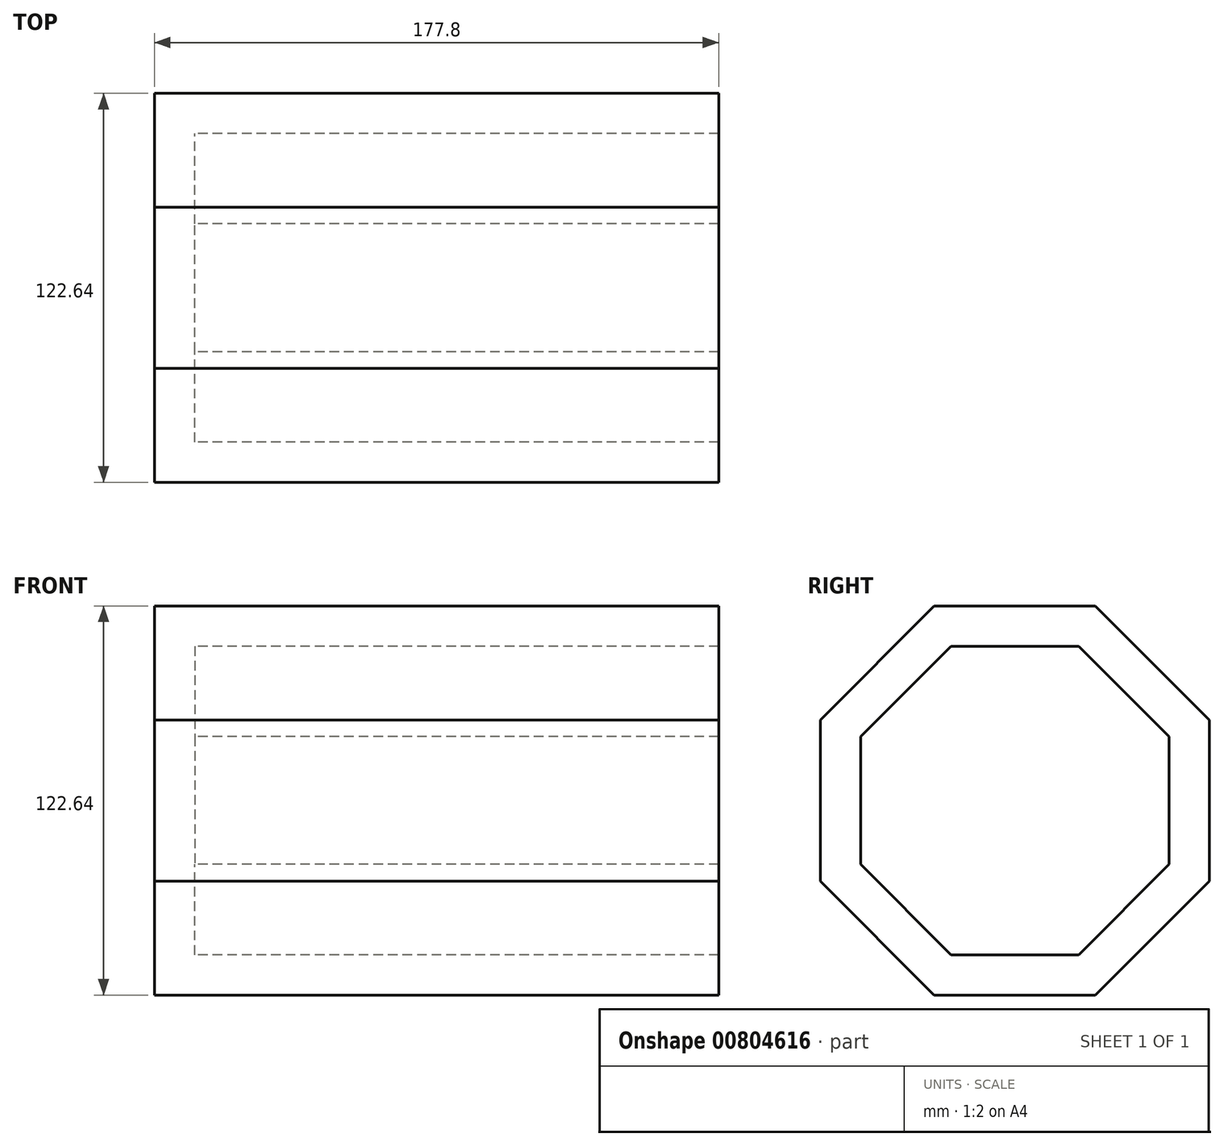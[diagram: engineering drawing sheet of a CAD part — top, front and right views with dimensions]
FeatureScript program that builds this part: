
annotation { "Feature Type Name" : "Feature", "Feature Type Description" : "" }
export const myFeature = defineFeature(function(context is Context, id is Id, definition is map)
    precondition{}
    {
        {
            var Q0;
            Q0=qCreatedBy(makeId("Right.planeOp"),FACE);
            var sketch = newSketch(context, id + "F0", { "sketchPlane" : qUnion([Q0])});
            skCircle(sketch, "E0.cCircle", {"center": v(0, 0) * mm, "radius": 61.32 * mm, "construction": true});
            skLineSegment(sketch, "E0.0", {"start": v(61.32, 25.4) * mm, "end": v(61.32, -25.4) * mm});
            skLineSegment(sketch, "E0.1", {"start": v(61.32, -25.4) * mm, "end": v(25.4, -61.32) * mm});
            skLineSegment(sketch, "E0.2", {"start": v(25.4, -61.32) * mm, "end": v(-25.4, -61.32) * mm});
            skLineSegment(sketch, "E0.3", {"start": v(-25.4, -61.32) * mm, "end": v(-61.32, -25.4) * mm});
            skLineSegment(sketch, "E0.4", {"start": v(-61.32, -25.4) * mm, "end": v(-61.32, 25.4) * mm});
            skLineSegment(sketch, "E0.5", {"start": v(-61.32, 25.4) * mm, "end": v(-25.4, 61.32) * mm});
            skLineSegment(sketch, "E0.6", {"start": v(-25.4, 61.32) * mm, "end": v(25.4, 61.32) * mm});
            skLineSegment(sketch, "E0.7", {"start": v(25.4, 61.32) * mm, "end": v(61.32, 25.4) * mm});
            skPoint(sketch, "E0.0.midPoint", {"position": v(61.32, 0) * mm});
            skSolve(sketch);
        }
        {
            var Q0;
            Q0=makeQuery(id+"F0.imprint","IMPRINT",FACE,{"disambiguationData":[TD([[makeQuery(id+"F0.imprint","IMPRINT",EDGE,{"derivedFrom":sQuery(id+"F0.wireOp",EDGE,"E0.0")}),-1.0]])]});
            extrude(context, id + "F1", {"entities" : qUnion([Q0]), "depth" : 177.8 * mm, "offsetDistance" : 25.4 * mm});
        }
        {
            var Q0;
            Q0=makeQuery(id+"F1.opExtrude","CAP_FACE",FACE,{"disambiguationData":[OSD([sQuery(id+"F0.wireOp",EDGE,"E0.0"),sQuery(id+"F0.wireOp",EDGE,"E0.1"),sQuery(id+"F0.wireOp",EDGE,"E0.2"),sQuery(id+"F0.wireOp",EDGE,"E0.3"),sQuery(id+"F0.wireOp",EDGE,"E0.4"),sQuery(id+"F0.wireOp",EDGE,"E0.5"),sQuery(id+"F0.wireOp",EDGE,"E0.6"),sQuery(id+"F0.wireOp",EDGE,"E0.7")])],"isStart":false});
            shell(context, id + "F2", {"entities" : qUnion([Q0]), "thickness" : 12.7 * mm});
        }
    });
